# Revit family: SANINDUSA_137021004_Sanibold_SaniboldFDclosecoupledtoilet360x640x395_V0
name_source: partatom
category: Plumbing Fixtures
revit_build: Autodesk Revit 2018 (Build: 20170223_1515(x64)
units: mm (PartAtom-declared; Revit-internal decimal feet)

## family parameters
Cut with Voids When Loaded = No
Host = Face
Part Type = Normal
Room Calculation Point = No
Round Connector Dimension = Use Diameter
Shared = No

## types (1)
- SANINDUSA_137021004_Sanibold_SaniboldFDclosecoupledtoilet360x640x395_V0
    AssetType = Fixed
    Color = white
    Constituents = Compatible toilet seats (not included): 23731 – Sanibold clipoff slowclose toilet seat; 23761 ‐ Slim clipoff slowclose Sanibold toilet seat (white); Compatible cisterns (not included): 137111LM ‐ Sanibold cistern with mechanism; 137113LM ‐ Sanibold cistern L/E with mechanism; 23-fixing kit (included); Pan connector code MSKT1714 (included).
    Default Elevation = 1219 mm
    Description = Soil appliance for the disposal of excrement.
    DrainSize = 90 mm  [stored 0.295276 ft]
    Element Type = TOILETPAN: Soil appliance for the disposal of excrement.
    Features = "Domestic and 
commercial use. Versatile timeless design. Seats with clipoff system easy to clean and slow close option. Back to wall WC."
    Finish = gloss
    InletDiameter = 0 mm  [stored 0 ft]
    Installation Instructions = https://www.tec.sanindusa.pt
    InstallationDate = 1900-12-31T23:59:59
    Manufacturer = Sanindusa
    ManufacturerName = Sanindusa
    ManufacturerURL = www.tec.sanindusa.pt
    Material = vitreous china
    Model = 137021004
    ModelNumber = 137021004
    ModelReference = Sanibold
    Name = Sanibold F|D close coupled toilet
    NominalHeight = 395 mm  [stored 1.29593 ft]
    NominalLength = 360 mm  [stored 1.1811 ft]
    NominalWidth = 640 mm  [stored 2.09974 ft]
    PanColor = white
    PanMaterial = vitreous china
    PanMounting = pedestal
    Pre-defined type (IFC) = TOILETPAN
    ProductInformation = https://www.tec.sanindusa.pt
    ProductionYear = 2017
    Size = 360x640x395
    ToiletPanType = washdown
    ToiletType = LooseCoupled
    Type (IFC) = IfcSanitaryTerminalType
    URL = www.tec.sanindusa.pt
    Uniclass2015Code = Pr_40_20_93_94
    Uniclass2015Title = WC pans
    Uniclass2015Version = Products v1.6
    Version = 1
    WarrantyDescription = https://www.tec.sanindusa.pt
    WarrantyDurationParts = 5
    WarrantyDurationUnit = year
    WarrantyStartDate = 1900-12-31T23:59:59
    Waste Connection = Yes
    Weight = 31.00 kg

note: [stored X ft] marks values corroborated as IEEE doubles in the binary element streams (Revit-internal decimal feet)

## geometry (parser evidence)
native form markers: Sweep x5
no freeform markers — native parametric forms only
